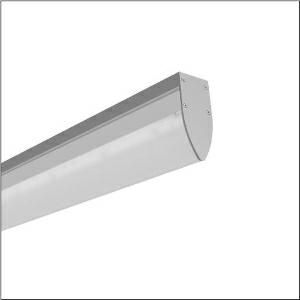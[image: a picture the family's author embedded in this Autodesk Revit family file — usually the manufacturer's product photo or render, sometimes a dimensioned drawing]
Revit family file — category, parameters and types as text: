
# Revit family: mira_r__21_td_51fr527p494a_f38a
name_source: partatom
category: Lighting Fixtures
units: mm (PartAtom-declared; Revit-internal decimal feet)

## family parameters
Cut with Voids When Loaded = No
Host = Face
Light Source = No
Part Type = Normal
Room Calculation Point = No
Round Connector Dimension = Use Diameter
Shared = No

## types (1)
- Mira® 21 TD (1 x LED, 9160 lm, 65 W, 4000K)
    Apparent Load = 65 VA
    CIE Flux Codes = 40 68 87 81 100
    Color Rendering = 80
    Color Temperature = 4000K
    Default Elevation = 1800 mm
    Description = Mira® 21 TD, clean room luminaire, primary light control with reflector, primary optical cover: cover, of PMMA, frosted, light emission: direct distribution, primary light characteristic: symmetric, installation type: surface-mounted, LED, rated luminous flux: 9.160lm, luminous efficacy: 141lm/W, light colour: 840, colour temperature: 4000K, control gear: ON/OFF, with terminal, 3-pole, max. 2.5mm², mains connection: 230V, AC, 50/60Hz, rated input power: 65W, luminaire housing, of sheet steel, coated, pure white (RAL 9010), length: 1.500mm, width: 55mm, height: 120mm, protection rating (complete): IP43, insulation class (complete): insulation class I (protective earthing), certification: CE, UKCA, permissible operating ambient temperature: -5..+40°C, standard: EN 50419, packaging unit: 1 piece
    Height = 120 mm
    Lamp = 1 x LED
    Lamp Light Flux = 9160 lm
    Lamp Power = 65 W
    Lamp count = 1
    Length = 1500 mm
    Luminous efficacy = 141 lm/W
    Manufacturer = Siteco
    ModVariant = No
    Model = 51FR527P494A
    Mounting Place = Ceiling
    Mounting Type = Surface mounted
    Number of Poles = 1
    OnlyDefault = Yes
    Power Factor = 1
    Product Name = Mira® 21 TD
    Product group = clean room luminaire | ceiling mounted
    ProductGroupID = 305
    Protection Class = Protection class I
    Protection Degree = IP 43
    RLX_Detail_Level = 1
    RLX_Emergency_Light_Flux = 0 lm
    RLX_Emergency_Type = 0
    RLX_Emergency_Type_DB = No
    RlxData = <blob elided: 25185 chars, md5=4fa4d5ad>
    Socket = socket
    Standby Power = 0 W
    System Light Flux = 9160 lm
    System Power = 65 W
    Type Comments = Product without accessories
    Type Image = l_1007115.jpg
    URL = http://relux.com
    VarID = ---
    Voltage = 0 V
    Weight = 0.00 kg
    Width = 55 mm

## geometry (parser evidence)
native form markers: Blend x4, Sweep x13
no freeform markers — native parametric forms only
